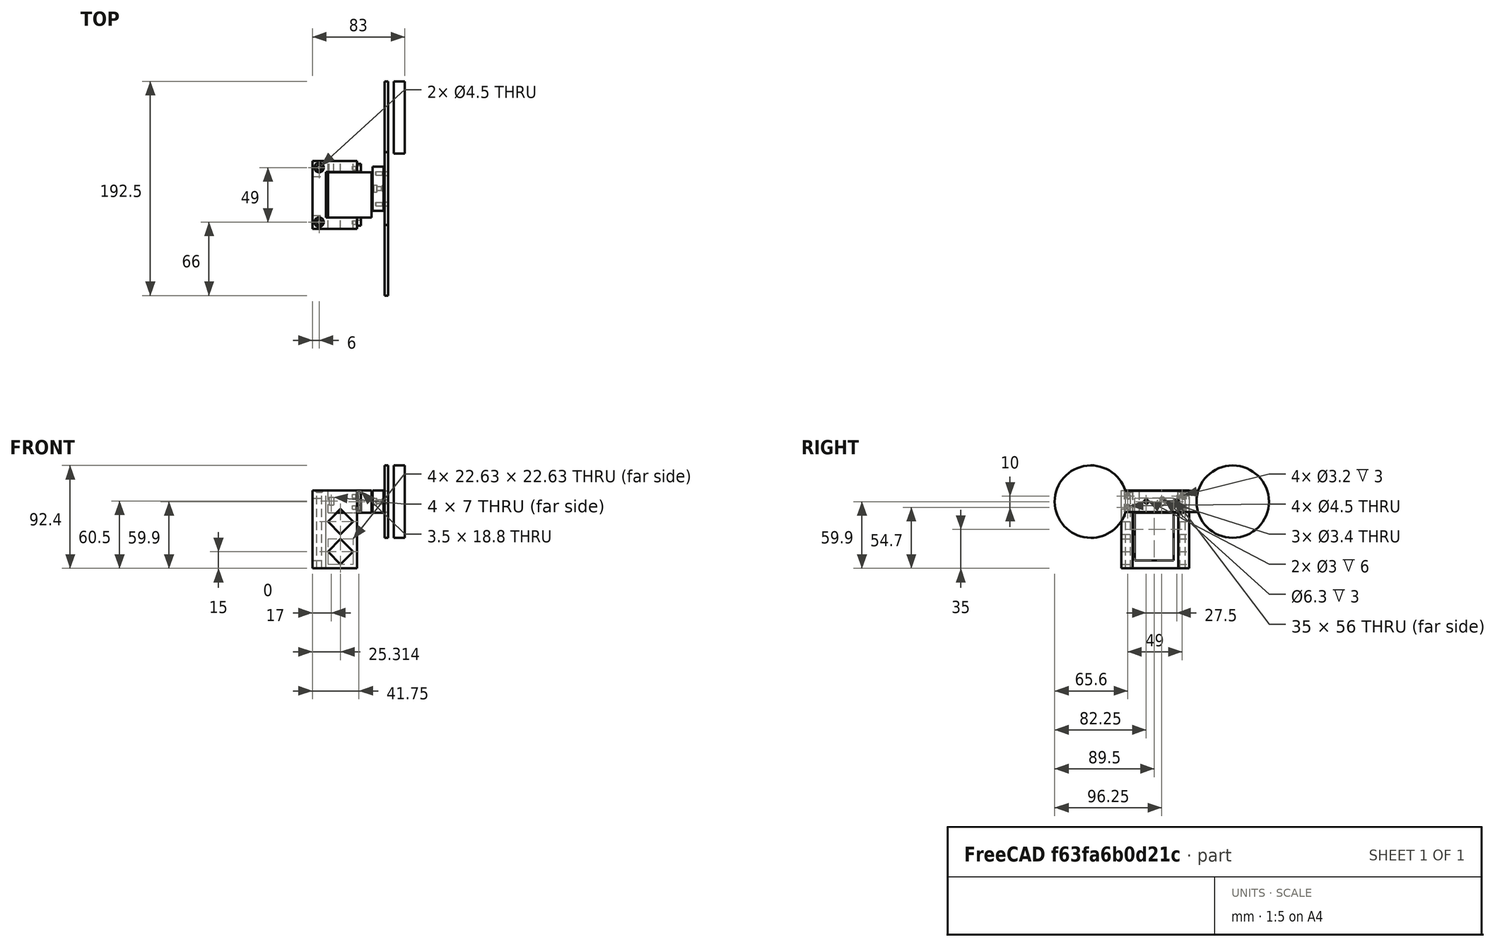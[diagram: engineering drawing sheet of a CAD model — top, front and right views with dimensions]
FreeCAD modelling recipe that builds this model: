
FCSTD DOCUMENT  (FreeCAD 0.19R24276 (Git))
Label: projector servo switch
License: All rights reserved
LicenseURL: http://en.wikipedia.org/wiki/All_rights_reserved
objects: Part::Cylinder×20, Part::Box×13, Part::Cut×12, Part::MultiFuse×11, Part::Chamfer×5, Part::Fuse×1, Part::Feature×1
note: 63 computed .brp shape members not serialized (recipe doc carries the construction recipe); baked Part::Feature solids carry a one-line shape summary decoded from their .brp

FEATURE [Part::Box] Box  label="Cube"
  AttacherType = Attacher::AttachEngine3D
  Height = 70
  Length = 40
  Width = 61
FEATURE [Part::Box] Box001  label="Cube001"
  AttacherType = Attacher::AttachEngine3D
  Height = 75
  Length = 28
  Placement = pos=(12,10,0) rot=(0,0,1;0rad)
  Width = 41
FEATURE [Part::Cut] Cut
  Base = -> Box
  Tool = -> Box001
FEATURE [Part::Box] Box002  label="Cube002"
  AttacherType = Attacher::AttachEngine3D
  Height = 19.8
  Length = 39
  Placement = pos=(14,10.25,50) rot=(0,0,1;0rad)
  Width = 40.5
FEATURE [Part::Box] Box003  label="Cube003"
  AttacherType = Attacher::AttachEngine3D
  Height = 18.8
  Length = 3.5
  Placement = pos=(40,2.75,50.5) rot=(0,0,1;0rad)
  Width = 7.5
FEATURE [Part::Box] Box004  label="Cube004"
  AttacherType = Attacher::AttachEngine3D
  Height = 18.8
  Length = 3.5
  Placement = pos=(40,50.75,50.5) rot=(0,0,1;0rad)
  Width = 7.5
FEATURE [Part::Cylinder] Cylinder
  Angle = 360
  AttacherType = Attacher::AttachEngine3D
  Height = 10
  Placement = pos=(36,5.6,64.7) rot=(0,1,0;1.5708rad)
  Radius = 2.25
FEATURE [Part::Cylinder] Cylinder001
  Angle = 360
  AttacherType = Attacher::AttachEngine3D
  Height = 10
  Placement = pos=(36,5.6,54.7) rot=(0,1,0;1.5708rad)
  Radius = 2.25
FEATURE [Part::Cylinder] Cylinder002
  Angle = 360
  AttacherType = Attacher::AttachEngine3D
  Height = 10
  Placement = pos=(36,54.6,64.7) rot=(0,1,0;1.5708rad)
  Radius = 2.25
FEATURE [Part::Cylinder] Cylinder003
  Angle = 360
  AttacherType = Attacher::AttachEngine3D
  Height = 10
  Placement = pos=(36,54.6,54.7) rot=(0,1,0;1.5708rad)
  Radius = 2.25
FEATURE [Part::Cylinder] Cylinder004
  Angle = 360
  AttacherType = Attacher::AttachEngine3D
  Height = 10
  Placement = pos=(45,36.25,59.9) rot=(0,1,0;1.5708rad)
  Radius = 2
FEATURE [Part::MultiFuse] Fusion
  Shapes = -> [Cylinder001,Cylinder]
FEATURE [Part::MultiFuse] Fusion001
  Shapes = -> [Cylinder002,Cylinder003]
FEATURE [Part::MultiFuse] Fusion002
  Shapes = -> [Box002,Box003,Box004]
FEATURE [Part::MultiFuse] Fusion003
  Shapes = -> [Fusion001,Fusion]
FEATURE [Part::Cut] Cut001
  Base = -> Fusion002
  Tool = -> Fusion003
FEATURE [Part::Cylinder] Cylinder005
  Angle = 360
  AttacherType = Attacher::AttachEngine3D
  Height = 10
  Placement = pos=(36,54.6,64.7) rot=(0,1,0;1.5708rad)
  Radius = 1.6
FEATURE [Part::Cylinder] Cylinder006
  Angle = 360
  AttacherType = Attacher::AttachEngine3D
  Height = 10
  Placement = pos=(36,54.6,54.7) rot=(0,1,0;1.5708rad)
  Radius = 1.6
FEATURE [Part::Cylinder] Cylinder007
  Angle = 360
  AttacherType = Attacher::AttachEngine3D
  Height = 10
  Placement = pos=(36,5.6,64.7) rot=(0,1,0;1.5708rad)
  Radius = 1.6
FEATURE [Part::Cylinder] Cylinder008
  Angle = 360
  AttacherType = Attacher::AttachEngine3D
  Height = 10
  Placement = pos=(36,5.6,54.7) rot=(0,1,0;1.5708rad)
  Radius = 1.6
FEATURE [Part::Box] Box005  label="Cube005"
  AttacherType = Attacher::AttachEngine3D
  Height = 7
  Length = 4
  Placement = pos=(15,49,57) rot=(0,0,1;0rad)
  Width = 16
FEATURE [Part::Fuse] Fusion004
  Base = -> Cylinder004
  Tool = -> Cut001
FEATURE [Part::MultiFuse] Fusion005
  Shapes = -> [Cylinder005,Cylinder006,Cylinder007,Cylinder008]
FEATURE [Part::Cut] Cut002
  Base = -> Cut
  Tool = -> Fusion005
FEATURE [Part::Cut] Cut003
  Base = -> Cut002
  Tool = -> Box005
FEATURE [Part::Cylinder] Cylinder009
  Angle = 360
  AttacherType = Attacher::AttachEngine3D
  Height = 74
  Placement = pos=(6,6,-2) rot=(0,0,1;0rad)
  Radius = 2.25
FEATURE [Part::Cylinder] Cylinder010
  Angle = 360
  AttacherType = Attacher::AttachEngine3D
  Height = 74
  Placement = pos=(6,55,-2) rot=(0,0,1;0rad)
  Radius = 2.25
FEATURE [Part::MultiFuse] Fusion006
  Shapes = -> [Cylinder009,Cylinder010]
FEATURE [Part::Cut] Cut004
  Base = -> Cut003
  Tool = -> Fusion006
FEATURE [Part::Chamfer] Chamfer
  Base = -> Cut004
  Edges = 2 edges r=2: [Edge14,Edge15]
FEATURE [Part::Box] Box006  label="Cube006"
  AttacherType = Attacher::AttachEngine3D
  Height = 20
  Length = 10
  Placement = pos=(54,16,50) rot=(0,0,1;0rad)
  Width = 40
FEATURE [Part::Cylinder] Cylinder011
  Angle = 360
  AttacherType = Attacher::AttachEngine3D
  Height = 10
  Placement = pos=(48,36.25,59.9) rot=(0,1,0;1.5708rad)
  Radius = 3.15
FEATURE [Part::Cut] Cut005
  Base = -> Box006
  Tool = -> Cylinder011
FEATURE [Part::Cylinder] Cylinder012
  Angle = 360
  AttacherType = Attacher::AttachEngine3D
  Height = 10
  Placement = pos=(57,36.25,59.9) rot=(0,1,0;1.5708rad)
  Radius = 1.7
FEATURE [Part::Cut] Cut006
  Base = -> Cut005
  Tool = -> Cylinder012
FEATURE [Part::Chamfer] Chamfer001
  Base = -> Cut006
  Edges = 1 edges r=2: [Edge16]
FEATURE [Part::Cylinder] Cylinder013
  Angle = 360
  AttacherType = Attacher::AttachEngine3D
  Height = 10
  Placement = pos=(57,49.75,59.9) rot=(0,1,0;1.5708rad)
  Radius = 1.5
FEATURE [Part::Cylinder] Cylinder014
  Angle = 360
  AttacherType = Attacher::AttachEngine3D
  Height = 10
  Placement = pos=(57,22.25,59.9) rot=(0,1,0;1.5708rad)
  Radius = 1.5
FEATURE [Part::MultiFuse] Fusion007
  Shapes = -> [Cylinder013,Cylinder014]
FEATURE [Part::Cut] Cut007
  Base = -> Chamfer001
  Tool = -> Fusion007
FEATURE [Part::Chamfer] Chamfer002
  Base = -> Cut007
  Edges = 2 edges r=1: [Edge5,Edge7]
FEATURE [Part::Box] Box007  label="Cube007"
  AttacherType = Attacher::AttachEngine3D
  Height = 19
  Length = 3
  Placement = pos=(65,-44,50.5) rot=(0,0,1;0rad)
  Width = 159
FEATURE [Part::Cylinder] Cylinder015
  Angle = 360
  AttacherType = Attacher::AttachEngine3D
  Height = 10
  Placement = pos=(73,100,59.9) rot=(0,1,0;1.5708rad)
  Radius = 32.5
FEATURE [Part::Cylinder] Cylinder016
  Angle = 360
  AttacherType = Attacher::AttachEngine3D
  Height = 3
  Placement = pos=(65,100,59.9) rot=(0,1,0;1.5708rad)
  Radius = 32.5
FEATURE [Part::Cylinder] Cylinder017
  Angle = 360
  AttacherType = Attacher::AttachEngine3D
  Height = 3
  Placement = pos=(65,-27.5,59.9) rot=(0,1,0;1.5708rad)
  Radius = 32.5
FEATURE [Part::Cylinder] Cylinder018
  Angle = 360
  AttacherType = Attacher::AttachEngine3D
  Height = 10
  Placement = pos=(62,22.25,59.9) rot=(0,1,0;1.5708rad)
  Radius = 1.7
FEATURE [Part::Cylinder] Cylinder019
  Angle = 360
  AttacherType = Attacher::AttachEngine3D
  Height = 10
  Placement = pos=(60,49.75,59.9) rot=(0,1,0;1.5708rad)
  Radius = 1.7
FEATURE [Part::MultiFuse] Fusion008
  Shapes = -> [Box007,Cylinder016,Cylinder017]
FEATURE [Part::MultiFuse] Fusion009
  Shapes = -> [Cylinder019,Cylinder018]
FEATURE [Part::Cut] Cut008
  Base = -> Fusion008
  Tool = -> Fusion009
FEATURE [Part::Feature] Cut008_cs
  Placement = pos=(0,0,0) rot=(0,1,0;1.5708rad)
  shape: bbox 65 x 192.5 x 3e-07 mm, 0 faces, 0 solids (baked)
FEATURE [Part::Chamfer] Chamfer003
  Base = -> Chamfer002
  Edges = 1 edges r=1: [Edge24]
FEATURE [Part::Chamfer] Chamfer004
  Base = -> Chamfer
  Edges = 4 edges r=1: [Edge22,Edge23,Edge38,Edge39]
FEATURE [Part::Box] Box008  label="Cube008"
  AttacherType = Attacher::AttachEngine3D
  Height = 56
  Length = 15
  Placement = pos=(-1,12,7) rot=(0,0,1;0rad)
  Width = 35
FEATURE [Part::Cut] Cut009
  Base = -> Chamfer004
  Tool = -> Box008
FEATURE [Part::Box] Box009  label="Cube009"
  AttacherType = Attacher::AttachEngine3D
  Height = 16
  Length = 16
  Placement = pos=(14,-1,15) rot=(0,1,0;0.785398rad)
  Width = 12
FEATURE [Part::Box] Box010  label="Cube010"
  AttacherType = Attacher::AttachEngine3D
  Height = 16
  Length = 16
  Placement = pos=(14,-1,42) rot=(0,1,0;0.785398rad)
  Width = 12
FEATURE [Part::MultiFuse] Fusion010
  Shapes = -> [Box009,Box010]
FEATURE [Part::Cut] Cut010
  Base = -> Cut009
  Tool = -> Fusion010
FEATURE [Part::Box] Box011  label="Cube011"
  AttacherType = Attacher::AttachEngine3D
  Height = 16
  Length = 16
  Placement = pos=(14,50,15) rot=(0,1,0;0.785398rad)
  Width = 12
FEATURE [Part::Box] Box012  label="Cube012"
  AttacherType = Attacher::AttachEngine3D
  Height = 16
  Length = 16
  Placement = pos=(14,50,42) rot=(0,1,0;0.785398rad)
  Width = 12
FEATURE [Part::MultiFuse] Fusion011
  Shapes = -> [Box011,Box012]
FEATURE [Part::Cut] Cut011
  Base = -> Cut010
  Tool = -> Fusion011
